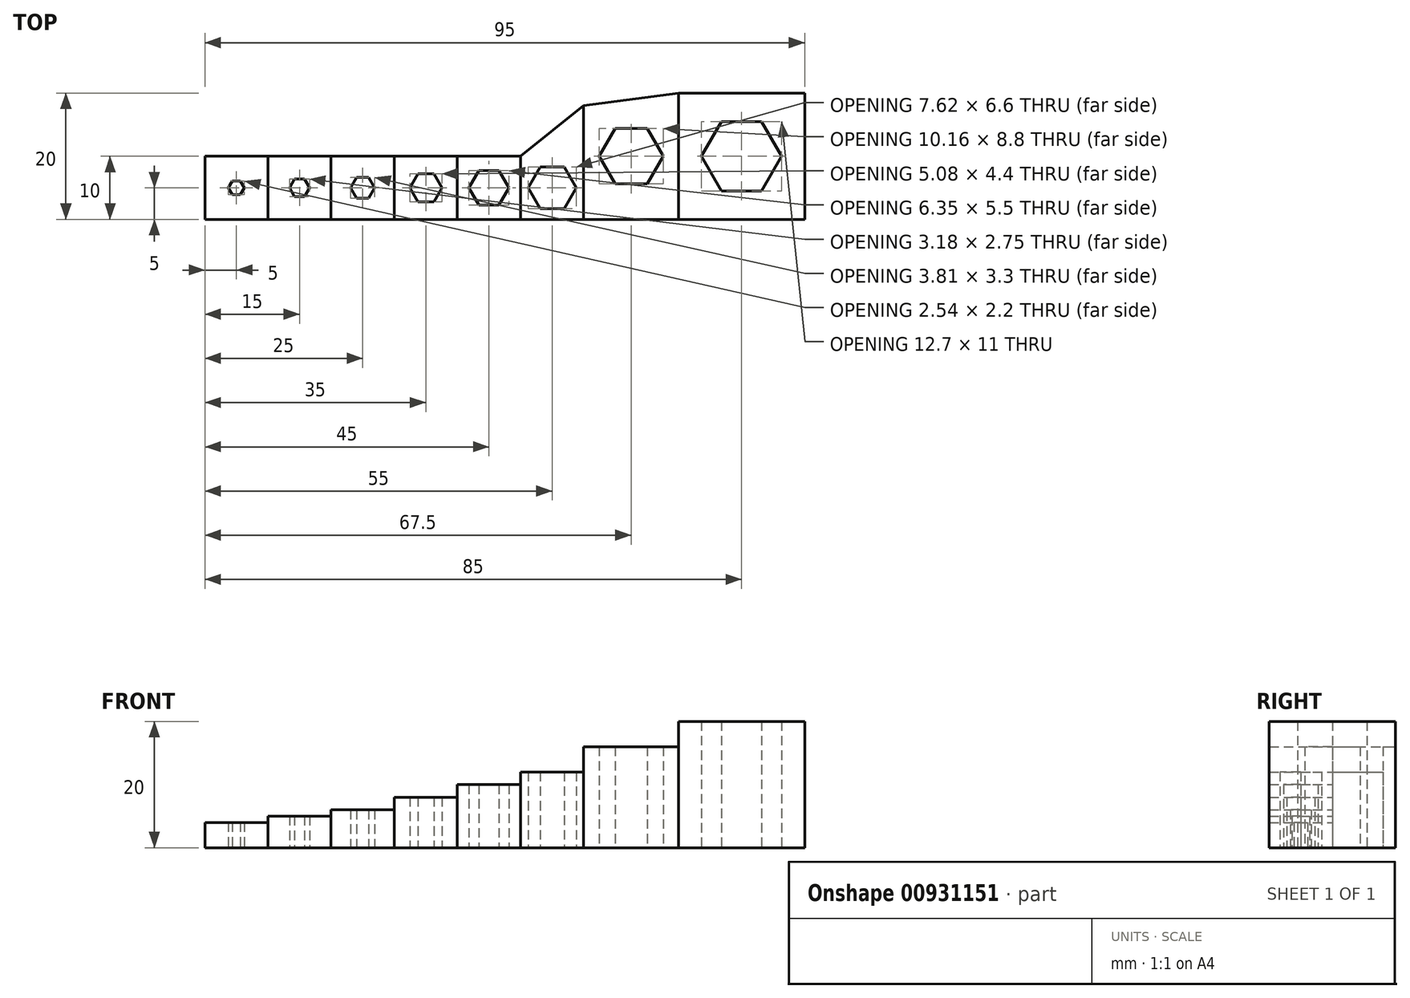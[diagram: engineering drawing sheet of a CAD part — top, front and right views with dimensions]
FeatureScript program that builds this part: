
annotation { "Feature Type Name" : "Feature", "Feature Type Description" : "" }
export const myFeature = defineFeature(function(context is Context, id is Id, definition is map)
    precondition{}
    {
        {
            assignVariable(context, id + "F0", {"name" : "HexSizeArray", "anyValue" : [2, 2.5, 3, 4, 5, 6, 8, 10]});
        }
        {
            assignVariable(context, id + "F1", {"name" : "DepthMulti", "anyValue" : 2});
        }
        {
            assignVariable(context, id + "F2", {"name" : "InsertionDepth", "anyValue" : [getVariable(context, 'HexSizeArray')[0] * getVariable(context, 'DepthMulti'), getVariable(context, 'HexSizeArray')[1] * getVariable(context, 'DepthMulti'), getVariable(context, 'HexSizeArray')[2] * getVariable(context, 'DepthMulti'), getVariable(context, 'HexSizeArray')[3] * getVariable(context, 'DepthMulti'), getVariable(context, 'HexSizeArray')[4] * getVariable(context, 'DepthMulti'), getVariable(context, 'HexSizeArray')[5] * getVariable(context, 'DepthMulti'), getVariable(context, 'HexSizeArray')[6] * getVariable(context, 'DepthMulti'), getVariable(context, 'HexSizeArray')[7] * getVariable(context, 'DepthMulti')]});
        }
        {
            var Q0;
            Q0=qCreatedBy(makeId("Top.planeOp"),FACE);
            var sketch = newSketch(context, id + "F3", { "sketchPlane" : qUnion([Q0])});
            skLineSegment(sketch, "E0", {"start": v(5.5, 0) * mm, "end": v(100.5, 0) * mm});
            skLineSegment(sketch, "E1", {"start": v(5.5, 0) * mm, "end": v(5.5, 10) * mm});
            skLineSegment(sketch, "E2", {"start": v(15.5, 0) * mm, "end": v(15.5, 10) * mm});
            skLineSegment(sketch, "E3", {"start": v(25.5, 0) * mm, "end": v(25.5, 10) * mm});
            skLineSegment(sketch, "E4", {"start": v(35.5, 0) * mm, "end": v(35.5, 10) * mm});
            skLineSegment(sketch, "E5", {"start": v(45.5, 0) * mm, "end": v(45.5, 10) * mm});
            skLineSegment(sketch, "E6", {"start": v(55.5, 0) * mm, "end": v(55.5, 10) * mm});
            skLineSegment(sketch, "E7", {"start": v(65.5, 0) * mm, "end": v(65.5, 18) * mm});
            skLineSegment(sketch, "E8", {"start": v(80.5, 0) * mm, "end": v(80.5, 20) * mm});
            skLineSegment(sketch, "E9", {"start": v(100.5, 0) * mm, "end": v(100.5, 20) * mm});
            skLineSegment(sketch, "E10", {"start": v(5.5, 10) * mm, "end": v(15.5, 10) * mm});
            skLineSegment(sketch, "E11", {"start": v(25.5, 10) * mm, "end": v(15.5, 10) * mm});
            skLineSegment(sketch, "E12", {"start": v(25.5, 10) * mm, "end": v(35.5, 10) * mm});
            skLineSegment(sketch, "E13", {"start": v(45.5, 10) * mm, "end": v(35.5, 10) * mm});
            skLineSegment(sketch, "E14", {"start": v(55.5, 10) * mm, "end": v(45.5, 10) * mm});
            skLineSegment(sketch, "E15", {"start": v(55.5, 10) * mm, "end": v(65.5, 18) * mm});
            skLineSegment(sketch, "E16", {"start": v(65.5, 18) * mm, "end": v(80.5, 20) * mm});
            skLineSegment(sketch, "E17", {"start": v(80.5, 20) * mm, "end": v(100.5, 20) * mm});
            skLineSegment(sketch, "E18", {"start": v(5.5, 10) * mm, "end": v(15.5, 0) * mm, "construction": true});
            skLineSegment(sketch, "E19", {"start": v(5.5, 0) * mm, "end": v(15.5, 10) * mm, "construction": true});
            skLineSegment(sketch, "E20", {"start": v(15.5, 10) * mm, "end": v(25.5, 0) * mm, "construction": true});
            skLineSegment(sketch, "E21", {"start": v(15.5, 0) * mm, "end": v(25.5, 10) * mm, "construction": true});
            skLineSegment(sketch, "E22", {"start": v(25.5, 0) * mm, "end": v(35.5, 10) * mm, "construction": true});
            skLineSegment(sketch, "E23", {"start": v(25.5, 10) * mm, "end": v(35.5, 0) * mm, "construction": true});
            skLineSegment(sketch, "E24", {"start": v(35.5, 0) * mm, "end": v(45.5, 10) * mm, "construction": true});
            skLineSegment(sketch, "E25", {"start": v(35.5, 10) * mm, "end": v(45.5, 0) * mm, "construction": true});
            skLineSegment(sketch, "E26", {"start": v(45.5, 0) * mm, "end": v(55.5, 10) * mm, "construction": true});
            skLineSegment(sketch, "E27", {"start": v(45.5, 10) * mm, "end": v(55.5, 0) * mm, "construction": true});
            skLineSegment(sketch, "E28", {"start": v(55.5, 10) * mm, "end": v(65.5, 0) * mm, "construction": true});
            skLineSegment(sketch, "E29", {"start": v(55.5, 0) * mm, "end": v(65.5, 10) * mm, "construction": true});
            skLineSegment(sketch, "E30", {"start": v(65.5, 18) * mm, "end": v(80.5, 0) * mm, "construction": true});
            skLineSegment(sketch, "E31", {"start": v(65.5, 0) * mm, "end": v(80.5, 20) * mm, "construction": true});
            skLineSegment(sketch, "E32", {"start": v(80.5, 20) * mm, "end": v(100.5, 0) * mm, "construction": true});
            skLineSegment(sketch, "E33", {"start": v(80.5, 0) * mm, "end": v(100.5, 20) * mm, "construction": true});
            skCircle(sketch, "E34.cCircle", {"center": v(10.5, 5) * mm, "radius": 1.1 * mm, "construction": true});
            skLineSegment(sketch, "E34.0", {"start": v(9.86, 6.1) * mm, "end": v(11.14, 6.1) * mm});
            skLineSegment(sketch, "E34.1", {"start": v(11.14, 6.1) * mm, "end": v(11.77, 5) * mm});
            skLineSegment(sketch, "E34.2", {"start": v(11.77, 5) * mm, "end": v(11.14, 3.9) * mm});
            skLineSegment(sketch, "E34.3", {"start": v(11.14, 3.9) * mm, "end": v(9.86, 3.9) * mm});
            skLineSegment(sketch, "E34.4", {"start": v(9.86, 3.9) * mm, "end": v(9.23, 5) * mm});
            skLineSegment(sketch, "E34.5", {"start": v(9.23, 5) * mm, "end": v(9.86, 6.1) * mm});
            skPoint(sketch, "E34.0.midPoint", {"position": v(10.5, 6.1) * mm});
            skCircle(sketch, "E35.cCircle", {"center": v(20.5, 5) * mm, "radius": 1.37 * mm, "construction": true});
            skLineSegment(sketch, "E35.0", {"start": v(19.7, 6.37) * mm, "end": v(21.3, 6.37) * mm});
            skLineSegment(sketch, "E35.1", {"start": v(21.3, 6.37) * mm, "end": v(22.09, 5) * mm});
            skLineSegment(sketch, "E35.2", {"start": v(22.09, 5) * mm, "end": v(21.3, 3.62) * mm});
            skLineSegment(sketch, "E35.3", {"start": v(21.3, 3.62) * mm, "end": v(19.7, 3.62) * mm});
            skLineSegment(sketch, "E35.4", {"start": v(19.7, 3.63) * mm, "end": v(18.91, 5) * mm});
            skLineSegment(sketch, "E35.5", {"start": v(18.91, 5) * mm, "end": v(19.7, 6.38) * mm});
            skPoint(sketch, "E35.0.midPoint", {"position": v(20.5, 6.37) * mm});
            skCircle(sketch, "E36.cCircle", {"center": v(30.5, 5) * mm, "radius": 1.65 * mm, "construction": true});
            skLineSegment(sketch, "E36.0", {"start": v(29.55, 6.65) * mm, "end": v(31.45, 6.65) * mm});
            skLineSegment(sketch, "E36.1", {"start": v(31.45, 6.65) * mm, "end": v(32.4, 5) * mm});
            skLineSegment(sketch, "E36.2", {"start": v(32.4, 5) * mm, "end": v(31.45, 3.35) * mm});
            skLineSegment(sketch, "E36.3", {"start": v(31.45, 3.35) * mm, "end": v(29.55, 3.35) * mm});
            skLineSegment(sketch, "E36.4", {"start": v(29.55, 3.35) * mm, "end": v(28.6, 5) * mm});
            skLineSegment(sketch, "E36.5", {"start": v(28.6, 5) * mm, "end": v(29.55, 6.65) * mm});
            skPoint(sketch, "E36.0.midPoint", {"position": v(30.5, 6.65) * mm});
            skCircle(sketch, "E37.cCircle", {"center": v(40.5, 5) * mm, "radius": 2.2 * mm, "construction": true});
            skLineSegment(sketch, "E37.0", {"start": v(39.23, 7.2) * mm, "end": v(41.77, 7.2) * mm});
            skLineSegment(sketch, "E37.1", {"start": v(41.77, 7.2) * mm, "end": v(43.04, 5) * mm});
            skLineSegment(sketch, "E37.2", {"start": v(43.04, 5) * mm, "end": v(41.77, 2.8) * mm});
            skLineSegment(sketch, "E37.3", {"start": v(41.77, 2.8) * mm, "end": v(39.23, 2.8) * mm});
            skLineSegment(sketch, "E37.4", {"start": v(39.23, 2.8) * mm, "end": v(37.96, 5) * mm});
            skLineSegment(sketch, "E37.5", {"start": v(37.96, 5) * mm, "end": v(39.23, 7.2) * mm});
            skPoint(sketch, "E37.0.midPoint", {"position": v(40.5, 7.2) * mm});
            skCircle(sketch, "E38.cCircle", {"center": v(50.5, 5) * mm, "radius": 2.75 * mm, "construction": true});
            skLineSegment(sketch, "E38.0", {"start": v(48.91, 7.75) * mm, "end": v(52.09, 7.75) * mm});
            skLineSegment(sketch, "E38.1", {"start": v(52.09, 7.75) * mm, "end": v(53.68, 5) * mm});
            skLineSegment(sketch, "E38.2", {"start": v(53.68, 5) * mm, "end": v(52.09, 2.25) * mm});
            skLineSegment(sketch, "E38.3", {"start": v(52.09, 2.25) * mm, "end": v(48.91, 2.25) * mm});
            skLineSegment(sketch, "E38.4", {"start": v(48.91, 2.25) * mm, "end": v(47.32, 5) * mm});
            skLineSegment(sketch, "E38.5", {"start": v(47.32, 5) * mm, "end": v(48.91, 7.75) * mm});
            skPoint(sketch, "E38.0.midPoint", {"position": v(50.5, 7.75) * mm});
            skCircle(sketch, "E39.cCircle", {"center": v(60.5, 5) * mm, "radius": 3.3 * mm, "construction": true});
            skLineSegment(sketch, "E39.0", {"start": v(58.6, 8.3) * mm, "end": v(62.4, 8.3) * mm});
            skLineSegment(sketch, "E39.1", {"start": v(62.4, 8.3) * mm, "end": v(64.31, 5) * mm});
            skLineSegment(sketch, "E39.2", {"start": v(64.31, 5) * mm, "end": v(62.4, 1.7) * mm});
            skLineSegment(sketch, "E39.3", {"start": v(62.4, 1.7) * mm, "end": v(58.6, 1.7) * mm});
            skLineSegment(sketch, "E39.4", {"start": v(58.6, 1.7) * mm, "end": v(56.69, 5) * mm});
            skLineSegment(sketch, "E39.5", {"start": v(56.69, 5) * mm, "end": v(58.6, 8.3) * mm});
            skPoint(sketch, "E39.0.midPoint", {"position": v(60.5, 8.3) * mm});
            skCircle(sketch, "E40.cCircle", {"center": v(73, 10) * mm, "radius": 4.4 * mm, "construction": true});
            skLineSegment(sketch, "E40.0", {"start": v(70.46, 14.4) * mm, "end": v(75.54, 14.4) * mm});
            skLineSegment(sketch, "E40.1", {"start": v(75.54, 14.4) * mm, "end": v(78.08, 10) * mm});
            skLineSegment(sketch, "E40.2", {"start": v(78.08, 10) * mm, "end": v(75.54, 5.6) * mm});
            skLineSegment(sketch, "E40.3", {"start": v(75.54, 5.6) * mm, "end": v(70.46, 5.6) * mm});
            skLineSegment(sketch, "E40.4", {"start": v(70.46, 5.6) * mm, "end": v(67.92, 10) * mm});
            skLineSegment(sketch, "E40.5", {"start": v(67.92, 10) * mm, "end": v(70.46, 14.4) * mm});
            skPoint(sketch, "E40.0.midPoint", {"position": v(73, 14.4) * mm});
            skCircle(sketch, "E41.cCircle", {"center": v(90.5, 10) * mm, "radius": 5.5 * mm, "construction": true});
            skLineSegment(sketch, "E41.0", {"start": v(87.32, 15.5) * mm, "end": v(93.68, 15.5) * mm});
            skLineSegment(sketch, "E41.1", {"start": v(93.68, 15.5) * mm, "end": v(96.85, 10) * mm});
            skLineSegment(sketch, "E41.2", {"start": v(96.85, 10) * mm, "end": v(93.68, 4.5) * mm});
            skLineSegment(sketch, "E41.3", {"start": v(93.68, 4.5) * mm, "end": v(87.32, 4.5) * mm});
            skLineSegment(sketch, "E41.4", {"start": v(87.32, 4.5) * mm, "end": v(84.15, 10) * mm});
            skLineSegment(sketch, "E41.5", {"start": v(84.15, 10) * mm, "end": v(87.32, 15.5) * mm});
            skPoint(sketch, "E41.0.midPoint", {"position": v(90.5, 15.5) * mm});
            skSolve(sketch);
        }
        {
            var Q0;
            {var subQ1=sQuery(id+"F3.wireOp",EDGE,"E1");Q0=makeQuery(id+"F3.imprint","IMPRINT",FACE,{"disambiguationData":[TD([[makeQuery(id+"F3.imprint","IMPRINT",EDGE,{"derivedFrom":subQ1}),-1.0]])]});}
            extrude(context, id + "F4", {"entities" : qUnion([Q0]), "depth" : (getVariable(context, 'InsertionDepth')[0]) * mm, "offsetDistance" : 25 * mm});
        }
        {
            var Q0;
            {var subQ1=sQuery(id+"F3.wireOp",EDGE,"E2");Q0=makeQuery(id+"F3.imprint","IMPRINT",FACE,{"disambiguationData":[TD([[makeQuery(id+"F3.imprint","IMPRINT",EDGE,{"derivedFrom":subQ1}),-1.0]])]});}
            extrude(context, id + "F5", {"entities" : qUnion([Q0]), "depth" : (getVariable(context, 'InsertionDepth')[1]) * mm, "offsetDistance" : 25 * mm});
        }
        {
            var Q0;
            {var subQ1=sQuery(id+"F3.wireOp",EDGE,"E3");Q0=makeQuery(id+"F3.imprint","IMPRINT",FACE,{"disambiguationData":[TD([[makeQuery(id+"F3.imprint","IMPRINT",EDGE,{"derivedFrom":subQ1}),-1.0]])]});}
            extrude(context, id + "F6", {"entities" : qUnion([Q0]), "depth" : (getVariable(context, 'InsertionDepth')[2]) * mm, "offsetDistance" : 25 * mm});
        }
        {
            var Q0;
            {var subQ1=sQuery(id+"F3.wireOp",EDGE,"E4");Q0=makeQuery(id+"F3.imprint","IMPRINT",FACE,{"disambiguationData":[TD([[makeQuery(id+"F3.imprint","IMPRINT",EDGE,{"derivedFrom":subQ1}),-1.0]])]});}
            extrude(context, id + "F7", {"entities" : qUnion([Q0]), "depth" : (getVariable(context, 'InsertionDepth')[3]) * mm, "offsetDistance" : 25 * mm});
        }
        {
            var Q0;
            {var subQ1=sQuery(id+"F3.wireOp",EDGE,"E5");Q0=makeQuery(id+"F3.imprint","IMPRINT",FACE,{"disambiguationData":[TD([[makeQuery(id+"F3.imprint","IMPRINT",EDGE,{"derivedFrom":subQ1}),-1.0]])]});}
            extrude(context, id + "F8", {"entities" : qUnion([Q0]), "depth" : (getVariable(context, 'InsertionDepth')[4]) * mm, "offsetDistance" : 25 * mm});
        }
        {
            var Q0;
            {var subQ1=sQuery(id+"F3.wireOp",EDGE,"E6");Q0=makeQuery(id+"F3.imprint","IMPRINT",FACE,{"disambiguationData":[TD([[makeQuery(id+"F3.imprint","IMPRINT",EDGE,{"derivedFrom":subQ1}),-1.0]])]});}
            extrude(context, id + "F9", {"entities" : qUnion([Q0]), "depth" : (getVariable(context, 'InsertionDepth')[5]) * mm, "offsetDistance" : 25 * mm});
        }
        {
            var Q0;
            {var subQ1=sQuery(id+"F3.wireOp",EDGE,"E7");Q0=makeQuery(id+"F3.imprint","IMPRINT",FACE,{"disambiguationData":[TD([[makeQuery(id+"F3.imprint","IMPRINT",EDGE,{"derivedFrom":subQ1}),-1.0]])]});}
            extrude(context, id + "F10", {"entities" : qUnion([Q0]), "depth" : (getVariable(context, 'InsertionDepth')[6]) * mm, "offsetDistance" : 25 * mm});
        }
        {
            var Q0;
            {var subQ1=sQuery(id+"F3.wireOp",EDGE,"E8");Q0=makeQuery(id+"F3.imprint","IMPRINT",FACE,{"disambiguationData":[TD([[makeQuery(id+"F3.imprint","IMPRINT",EDGE,{"derivedFrom":subQ1}),-1.0]])]});}
            extrude(context, id + "F11", {"entities" : qUnion([Q0]), "depth" : (getVariable(context, 'InsertionDepth')[7]) * mm, "offsetDistance" : 25 * mm});
        }
    });
